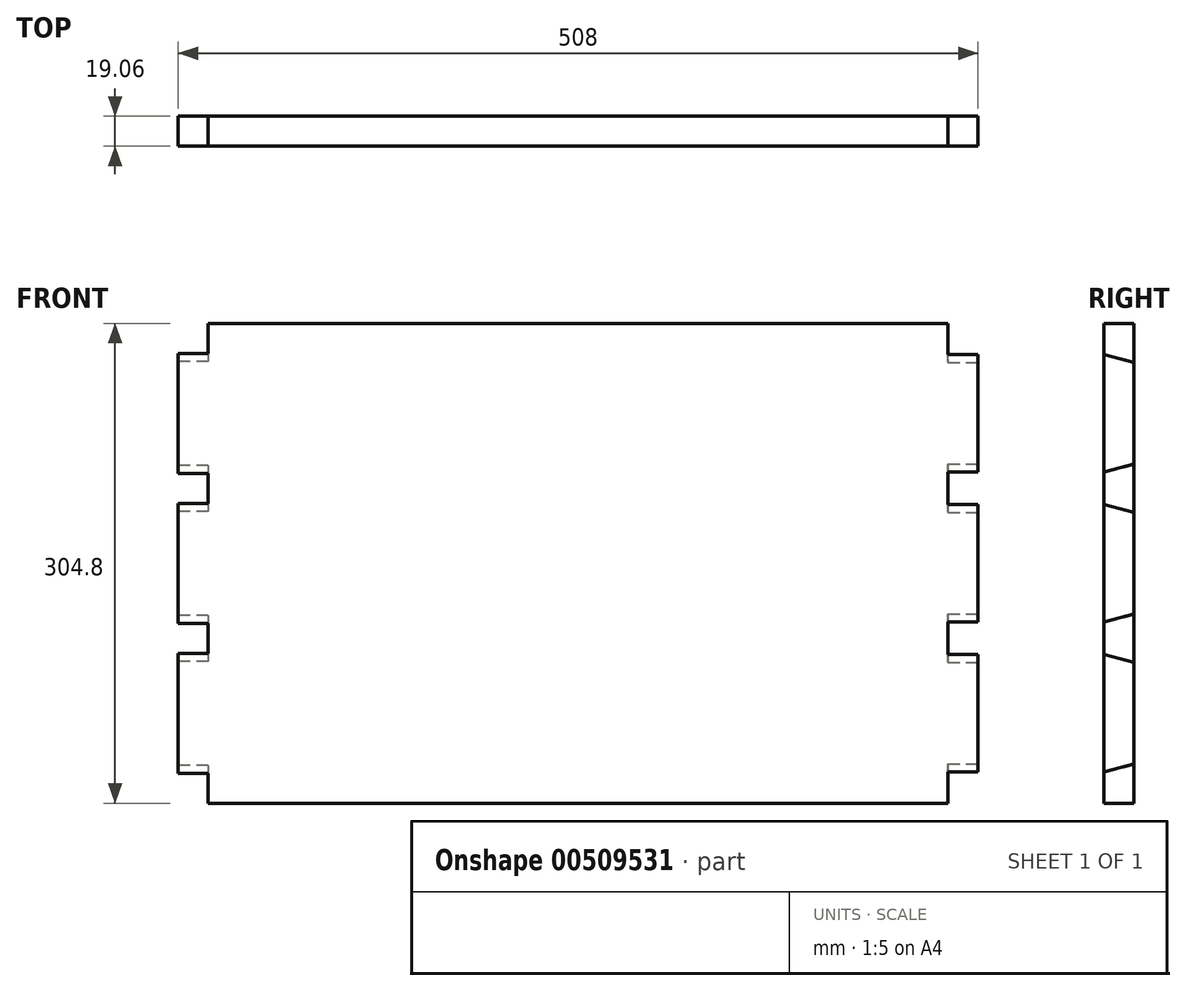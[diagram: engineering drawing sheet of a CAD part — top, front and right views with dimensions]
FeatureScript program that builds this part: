
annotation { "Feature Type Name" : "Feature", "Feature Type Description" : "" }
export const myFeature = defineFeature(function(context is Context, id is Id, definition is map)
    precondition{}
    {
        {
            var Q0;
            Q0=qCreatedBy(makeId("Front.planeOp"),FACE);
            var sketch = newSketch(context, id + "F0", { "sketchPlane" : qUnion([Q0])});
            skLineSegment(sketch, "E0.bottom", {"start": v(-254, 152.4) * mm, "end": v(254, 152.4) * mm});
            skLineSegment(sketch, "E0.top", {"start": v(-254, -152.4) * mm, "end": v(254, -152.4) * mm});
            skLineSegment(sketch, "E0.left", {"start": v(-254, 152.4) * mm, "end": v(-254, -152.4) * mm});
            skLineSegment(sketch, "E0.right", {"start": v(254, 152.4) * mm, "end": v(254, -152.4) * mm});
            skPoint(sketch, "E0.middle", {"position": v(0, 0) * mm});
            skSolve(sketch);
        }
        {
            var Q0;
            Q0=makeQuery(id+"F0.imprint","IMPRINT",FACE,{"disambiguationData":[TD([[makeQuery(id+"F0.imprint","IMPRINT",EDGE,{"derivedFrom":sQuery(id+"F0.wireOp",EDGE,"E0.bottom")}),-1.0]])]});
            extrude(context, id + "F1", {"entities" : qUnion([Q0]), "endBound" : BoundingType.SYMMETRIC, "depth" : 19.05 * mm, "offsetDistance" : 25.4 * mm});
        }
        {
            var Q0;
            Q0=makeQuery(id+"F1.opExtrude","SWEPT_FACE",FACE,{"disambiguationData":[OSD([sQuery(id+"F0.wireOp",EDGE,"E0.left")])]});
            var sketch = newSketch(context, id + "F2", { "sketchPlane" : qUnion([Q0])});
            skLineSegment(sketch, "E1", {"start": v(9.53, 133.35) * mm, "end": v(-9.53, 128.25) * mm});
            skLineSegment(sketch, "E2", {"start": v(-9.53, 128.25) * mm, "end": v(-9.53, 62.25) * mm});
            skLineSegment(sketch, "E3", {"start": v(-9.53, 62.25) * mm, "end": v(9.53, 57.15) * mm});
            skLineSegment(sketch, "E4", {"start": v(9.53, 57.15) * mm, "end": v(9.53, 133.35) * mm});
            skLineSegment(sketch, "E5", {"start": v(9.53, 38.1) * mm, "end": v(-9.53, 33) * mm});
            skLineSegment(sketch, "E6", {"start": v(-9.53, 33) * mm, "end": v(-9.53, -33) * mm});
            skLineSegment(sketch, "E7", {"start": v(-9.53, -33) * mm, "end": v(9.52, -38.1) * mm});
            skLineSegment(sketch, "E8", {"start": v(9.52, -38.1) * mm, "end": v(9.52, 38.1) * mm});
            skLineSegment(sketch, "E9", {"start": v(9.53, -57.15) * mm, "end": v(-9.52, -62.25) * mm});
            skLineSegment(sketch, "E10", {"start": v(-9.53, -62.25) * mm, "end": v(-9.53, -128.25) * mm});
            skLineSegment(sketch, "E11", {"start": v(-9.52, -128.25) * mm, "end": v(9.53, -133.35) * mm});
            skLineSegment(sketch, "E12", {"start": v(9.53, -133.35) * mm, "end": v(9.53, -57.15) * mm});
            skSolve(sketch);
        }
        {
            var Q0;
            {var subQ0=sQuery(id+"F2.wireOp",EDGE,"E1");Q0=makeQuery(id+"F2.imprint","IMPRINT",FACE,{"disambiguationData":[TD([[makeQuery(id+"F2.imprint","IMPRINT",EDGE,{"derivedFrom":subQ0}),-1.0]])]});}
            var Q1;
            {var subQ0=sQuery(id+"F2.wireOp",EDGE,"E3");Q1=makeQuery(id+"F2.imprint","IMPRINT",FACE,{"disambiguationData":[TD([[makeQuery(id+"F2.imprint","IMPRINT",EDGE,{"derivedFrom":subQ0}),-1.0]])]});}
            var Q2;
            {var subQ0=sQuery(id+"F2.wireOp",EDGE,"pdbCHJCJ-43zf-Y89S-envN-ZynBdgWXXw0p");Q2=makeQuery(id+"F2.imprint","IMPRINT",FACE,{"disambiguationData":[TD([[makeQuery(id+"F2.imprint","IMPRINT",EDGE,{"derivedFrom":subQ0}),-1.0]])]});}
            var Q3;
            {var subQ0=sQuery(id+"F2.wireOp",EDGE,"E7");Q3=makeQuery(id+"F2.imprint","IMPRINT",FACE,{"disambiguationData":[TD([[makeQuery(id+"F2.imprint","IMPRINT",EDGE,{"derivedFrom":subQ0}),-1.0]])]});}
            var Q4;
            {var subQ0=sQuery(id+"F2.wireOp",EDGE,"SS6ovqlH-G5il-ii56-CBag-bnnzi03IWFTy");Q4=makeQuery(id+"F2.imprint","IMPRINT",FACE,{"disambiguationData":[TD([[makeQuery(id+"F2.imprint","IMPRINT",EDGE,{"derivedFrom":subQ0}),-1.0]])]});}
            var Q5;
            {var subQ0=sQuery(id+"F2.wireOp",EDGE,"E11");Q5=makeQuery(id+"F2.imprint","IMPRINT",FACE,{"disambiguationData":[TD([[makeQuery(id+"F2.imprint","IMPRINT",EDGE,{"derivedFrom":subQ0}),-1.0]])]});}
            extrude(context, id + "F3", {"entities" : qUnion([Q0, Q1, Q2, Q3, Q4, Q5]), "operationType" : NewBodyOperationType.REMOVE, "oppositeDirection" : true, "depth" : 19.05 * mm, "offsetDistance" : 25.4 * mm});
        }
        {
            var Q0;
            Q0=makeQuery(id+"F1.opExtrude","SWEPT_FACE",FACE,{"disambiguationData":[OSD([sQuery(id+"F0.wireOp",EDGE,"E0.right")])]});
            var sketch = newSketch(context, id + "F4", { "sketchPlane" : qUnion([Q0])});
            skLineSegment(sketch, "E13", {"start": v(12.7, 126.54) * mm, "end": v(-12.7, 133.35) * mm});
            skLineSegment(sketch, "E14", {"start": v(-12.7, 133.35) * mm, "end": v(-12.7, 57.15) * mm});
            skLineSegment(sketch, "E15", {"start": v(-12.7, 57.15) * mm, "end": v(12.7, 63.96) * mm});
            skLineSegment(sketch, "E16", {"start": v(12.7, 63.96) * mm, "end": v(12.7, 126.54) * mm});
            skLineSegment(sketch, "E17", {"start": v(12.7, 31.3) * mm, "end": v(-12.7, 38.1) * mm});
            skLineSegment(sketch, "E18", {"start": v(-12.7, 38.1) * mm, "end": v(-12.7, -38.1) * mm});
            skLineSegment(sketch, "E19", {"start": v(-12.7, -38.1) * mm, "end": v(12.7, -31.3) * mm});
            skLineSegment(sketch, "E20", {"start": v(12.7, -31.3) * mm, "end": v(12.7, 31.3) * mm});
            skLineSegment(sketch, "E21", {"start": v(12.7, -63.96) * mm, "end": v(-12.7, -57.15) * mm});
            skLineSegment(sketch, "E22", {"start": v(-12.7, -57.15) * mm, "end": v(-12.7, -133.35) * mm});
            skLineSegment(sketch, "E23", {"start": v(-12.7, -133.35) * mm, "end": v(12.7, -126.54) * mm});
            skLineSegment(sketch, "E24", {"start": v(12.7, -126.54) * mm, "end": v(12.7, -63.96) * mm});
            skSolve(sketch);
        }
        {
            var Q0;
            {var subQ0=sQuery(id+"F4.wireOp",EDGE,"E13");Q0=makeQuery(id+"F4.imprint","IMPRINT",FACE,{"disambiguationData":[TD([[makeQuery(id+"F4.imprint","IMPRINT",EDGE,{"derivedFrom":subQ0}),-1.0]])]});}
            var Q1;
            {var subQ0=sQuery(id+"F4.wireOp",EDGE,"E15");Q1=makeQuery(id+"F4.imprint","IMPRINT",FACE,{"disambiguationData":[TD([[makeQuery(id+"F4.imprint","IMPRINT",EDGE,{"derivedFrom":subQ0}),-1.0]])]});}
            var Q2;
            {var subQ0=sQuery(id+"F4.wireOp",EDGE,"81f7bab2-2378-49b4-acbd-d895500fe6f5");Q2=makeQuery(id+"F4.imprint","IMPRINT",FACE,{"disambiguationData":[TD([[makeQuery(id+"F4.imprint","IMPRINT",EDGE,{"derivedFrom":subQ0}),-1.0]])]});}
            var Q3;
            {var subQ0=sQuery(id+"F4.wireOp",EDGE,"E19");Q3=makeQuery(id+"F4.imprint","IMPRINT",FACE,{"disambiguationData":[TD([[makeQuery(id+"F4.imprint","IMPRINT",EDGE,{"derivedFrom":subQ0}),-1.0]])]});}
            var Q4;
            {var subQ0=sQuery(id+"F4.wireOp",EDGE,"39ab3f0c-da6c-4b60-a77f-2a3094f85c7f");Q4=makeQuery(id+"F4.imprint","IMPRINT",FACE,{"disambiguationData":[TD([[makeQuery(id+"F4.imprint","IMPRINT",EDGE,{"derivedFrom":subQ0}),-1.0]])]});}
            var Q5;
            {var subQ0=sQuery(id+"F4.wireOp",EDGE,"E23");Q5=makeQuery(id+"F4.imprint","IMPRINT",FACE,{"disambiguationData":[TD([[makeQuery(id+"F4.imprint","IMPRINT",EDGE,{"derivedFrom":subQ0}),-1.0]])]});}
            extrude(context, id + "F5", {"entities" : qUnion([Q0, Q1, Q2, Q3, Q4, Q5]), "operationType" : NewBodyOperationType.REMOVE, "oppositeDirection" : true, "depth" : 19.05 * mm, "offsetDistance" : 25.4 * mm});
        }
    });
